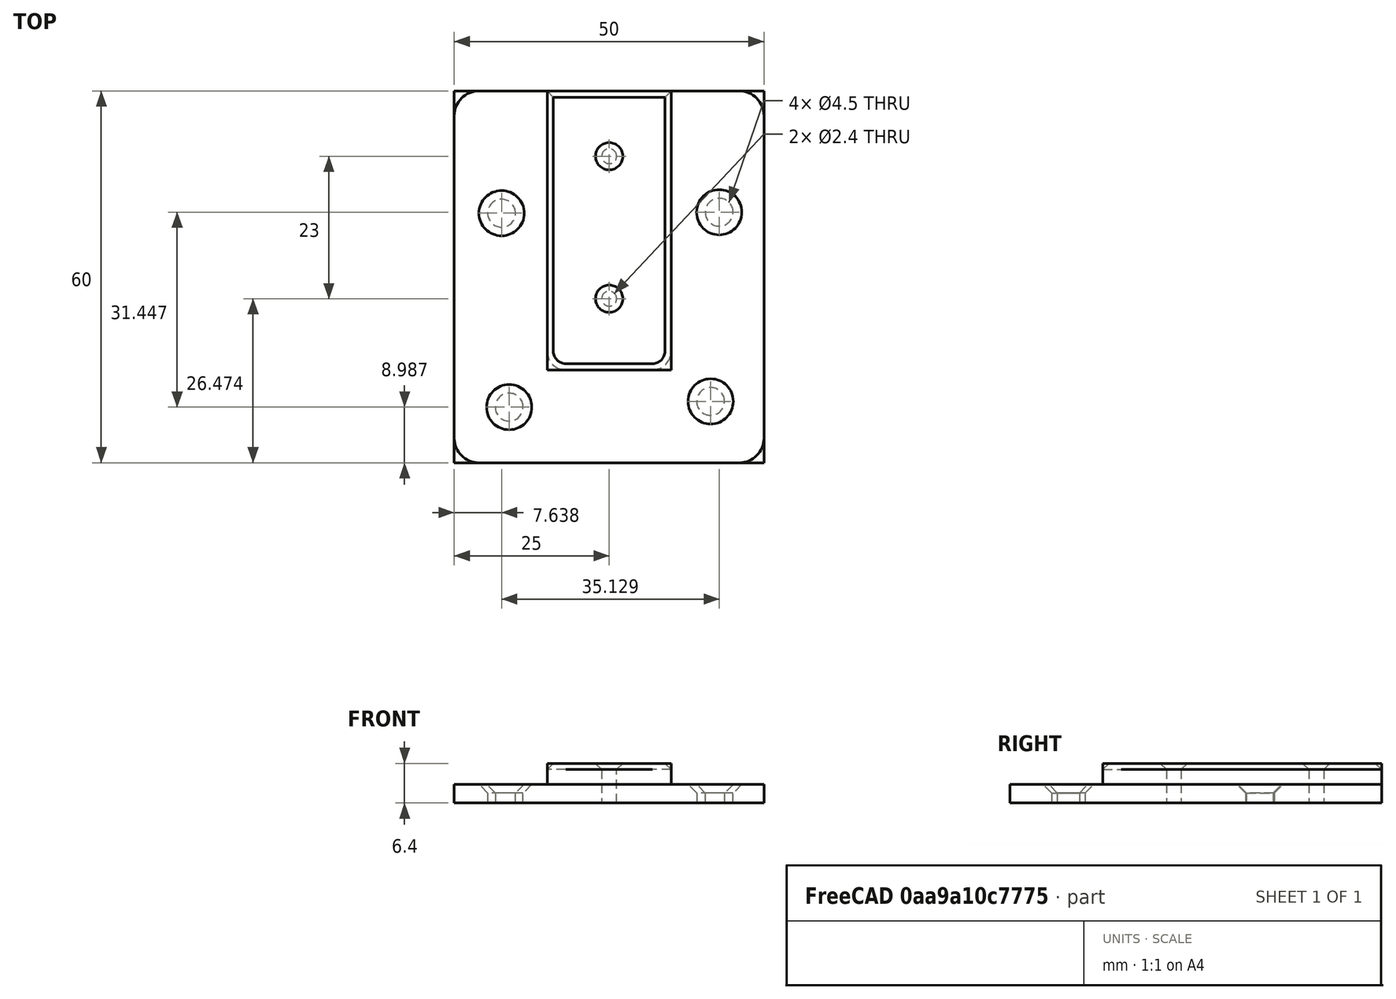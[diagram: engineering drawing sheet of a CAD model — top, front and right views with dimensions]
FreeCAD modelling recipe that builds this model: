
FCSTD DOCUMENT  (FreeCAD 0.16R)
Label: woldmarketpads
License: All rights reserved
LicenseURL: http://en.wikipedia.org/wiki/All_rights_reserved
objects: Sketcher::SketchObject×3, PartDesign::Pad×2, PartDesign::Fillet×2, PartDesign::Chamfer×2, PartDesign::Pocket×1, Mesh::Feature×1
note: 13 computed .brp shape members not serialized (recipe doc carries the construction recipe); baked Part::Feature solids carry a one-line shape summary decoded from their .brp

FEATURE [Sketcher::SketchObject] Sketch002
  Placement = pos=(0,0,0) rot=(1,0,0;3.14159rad)
  sketch-geometry (4):
    g0: LineSegment StartX=-25 StartY=37.5 StartZ=0 EndX=25 EndY=37.5 EndZ=0
    g1: LineSegment StartX=25 StartY=37.5 StartZ=0 EndX=25 EndY=-22.5 EndZ=0
    g2: LineSegment StartX=25 StartY=-22.5 StartZ=0 EndX=-25 EndY=-22.5 EndZ=0
    g3: LineSegment StartX=-25 StartY=-22.5 StartZ=0 EndX=-25 EndY=37.5 EndZ=0
  constraints (11):
    c: Coincident(g0,g1)
    c: Coincident(g1,g2)
    c: Coincident(g2,g3)
    c: Coincident(g3,g0)
    c: Horizontal(g0)
    c: Horizontal(g2)
    c: Vertical(g1)
    c: Vertical(g3)
    c: Symmetric(g0,g0,g-2)
    c: Distance(g0) = 50
    c: Distance(g1) = 60
FEATURE [PartDesign::Pad] Pad
  Length = 3
  Length2 = 100
  Placement = pos=(0,0,0) rot=(1,0,0;3.14159rad)
  Sketch = -> Sketch002
  Type = 0
FEATURE [Sketcher::SketchObject] Sketch
  Support = -> Pad [Face5]
  sketch-geometry (4):
    g0: LineSegment StartX=-10 StartY=22.5 StartZ=0 EndX=10 EndY=22.5 EndZ=0
    g1: LineSegment StartX=10 StartY=22.5 StartZ=0 EndX=10 EndY=-22.5 EndZ=0
    g2: LineSegment StartX=10 StartY=-22.5 StartZ=0 EndX=-10 EndY=-22.5 EndZ=0
    g3: LineSegment StartX=-10 StartY=-22.5 StartZ=0 EndX=-10 EndY=22.5 EndZ=0
  constraints (11):
    c: Coincident(g0,g1)
    c: Coincident(g1,g2)
    c: Coincident(g2,g3)
    c: Coincident(g3,g0)
    c: Horizontal(g0)
    c: Horizontal(g2)
    c: Vertical(g1)
    c: Vertical(g3)
    c: Symmetric(g1,g0,g-1)
    c: Distance(g0) = 20
    c: Distance(g1) = 45
FEATURE [PartDesign::Pad] Pad001
  Length = 3.4
  Length2 = 100
  Placement = pos=(0,0,0) rot=(1,0,0;3.14159rad)
  Sketch = -> Sketch
  Type = 0
FEATURE [Sketcher::SketchObject] Sketch001
  Placement = pos=(0,0,-3) rot=(1,0,0;3.14159rad)
  Support = -> Pad001 [Face5]
  sketch-geometry (6):
    g0: Circle CenterX=0 CenterY=11.0256 CenterZ=0 NormalX=0 NormalY=0 NormalZ=1 Radius=1.2
    g1: Circle CenterX=0 CenterY=-11.9744 CenterZ=0 NormalX=0 NormalY=0 NormalZ=1 Radius=1.2
    g2: Circle CenterX=16.3857 CenterY=27.5928 CenterZ=0 NormalX=0 NormalY=0 NormalZ=1 Radius=2.25
    g3: Circle CenterX=-17.3623 CenterY=-2.78042 CenterZ=0 NormalX=0 NormalY=0 NormalZ=1 Radius=2.25
    g4: Circle CenterX=-16.1351 CenterY=28.5132 CenterZ=0 NormalX=0 NormalY=0 NormalZ=1 Radius=2.25
    g5: Circle CenterX=17.7663 CenterY=-2.93383 CenterZ=0 NormalX=0 NormalY=0 NormalZ=1 Radius=2.25
  constraints (9):
    c: Distance(g1,g0) = 23
    c: Radius(g0) = 1.2
    c: Radius(g1) = 1.2
    c: PointOnObject(g0,g-2)
    c: PointOnObject(g1,g-2)
    c: Radius(g3) = 2.25
    c: Equal(g3,g4)
    c: Equal(g3,g2)
    c: Equal(g3,g5)
FEATURE [PartDesign::Pocket] Pocket
  Length = 5
  Placement = pos=(0,0,0) rot=(1,0,0;3.14159rad)
  Sketch = -> Sketch001
  Type = 1
FEATURE [PartDesign::Fillet] Fillet
  Base = -> Pocket [Edge5,Edge1,Edge2,Edge8]
  Placement = pos=(0,0,0) rot=(1,0,0;3.14159rad)
  Radius = 4
FEATURE [PartDesign::Fillet] Fillet001
  Base = -> Fillet [Edge42,Edge39]
  Placement = pos=(0,0,0) rot=(1,0,0;3.14159rad)
  Radius = 3
FEATURE [PartDesign::Chamfer] Chamfer
  Base = -> Fillet001 [Edge21,Edge23,Edge55,Edge29,Edge37,Edge33,Edge56,Edge57]
  Placement = pos=(0,0,0) rot=(1,0,0;3.14159rad)
  Size = 1
FEATURE [PartDesign::Chamfer] Chamfer001
  Base = -> Chamfer [Edge24,Edge23,Edge26,Edge25]
  Placement = pos=(0,0,0) rot=(1,0,0;3.14159rad)
  Size = 1.4
FEATURE [Mesh::Feature] Mesh  label="Chamfer001 (Meshed)"
